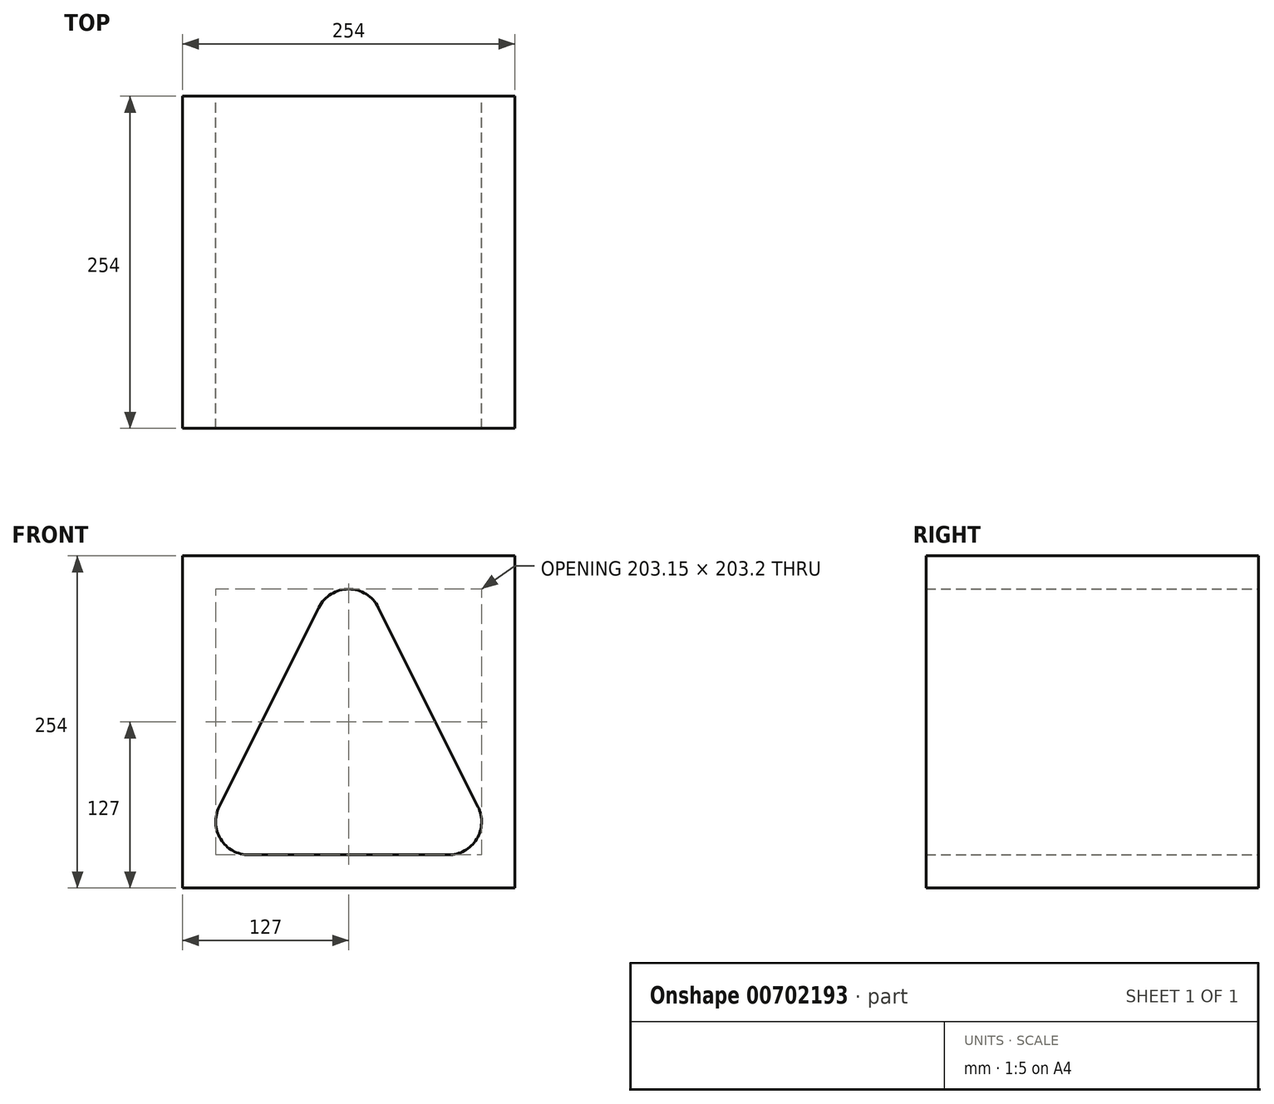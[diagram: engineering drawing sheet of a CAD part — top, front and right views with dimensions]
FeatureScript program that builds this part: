
annotation { "Feature Type Name" : "Feature", "Feature Type Description" : "" }
export const myFeature = defineFeature(function(context is Context, id is Id, definition is map)
    precondition{}
    {
        {
            var Q0;
            Q0=qCreatedBy(makeId("Front.planeOp"),FACE);
            var sketch = newSketch(context, id + "F0", { "sketchPlane" : qUnion([Q0])});
            skLineSegment(sketch, "E0", {"start": v(0, 0) * mm, "end": v(254, 0) * mm});
            skLineSegment(sketch, "E1", {"start": v(254, 0) * mm, "end": v(254, 254) * mm});
            skLineSegment(sketch, "E2", {"start": v(254, 254) * mm, "end": v(0, 254) * mm});
            skLineSegment(sketch, "E3", {"start": v(0, 254) * mm, "end": v(0, 0) * mm});
            skArc(sketch, "E4", {"start": v(28.08, 62.16) * mm, "mid": v(29.2, 37.45) * mm, "end": v(50.8, 25.4) * mm});
            skArc(sketch, "E5", {"start": v(203.2, 25.4) * mm, "mid": v(224.8, 37.45) * mm, "end": v(225.92, 62.16) * mm});
            skArc(sketch, "E6", {"start": v(149.72, 214.56) * mm, "mid": v(127, 228.6) * mm, "end": v(104.28, 214.56) * mm});
            skLineSegment(sketch, "E7", {"start": v(104.28, 214.56) * mm, "end": v(28.08, 62.16) * mm});
            skLineSegment(sketch, "E8", {"start": v(149.72, 214.56) * mm, "end": v(225.92, 62.16) * mm});
            skLineSegment(sketch, "E9", {"start": v(50.8, 25.4) * mm, "end": v(203.2, 25.4) * mm});
            skSolve(sketch);
        }
        {
            var Q0;
            Q0=makeQuery(id+"F0.imprint","IMPRINT",FACE,{"disambiguationData":[TD([[makeQuery(id+"F0.imprint","IMPRINT",EDGE,{"derivedFrom":sQuery(id+"F0.wireOp",EDGE,"E0")}),1.0]])]});
            extrude(context, id + "F1", {"entities" : qUnion([Q0]), "depth" : 254 * mm, "offsetDistance" : 25.4 * mm});
        }
    });
